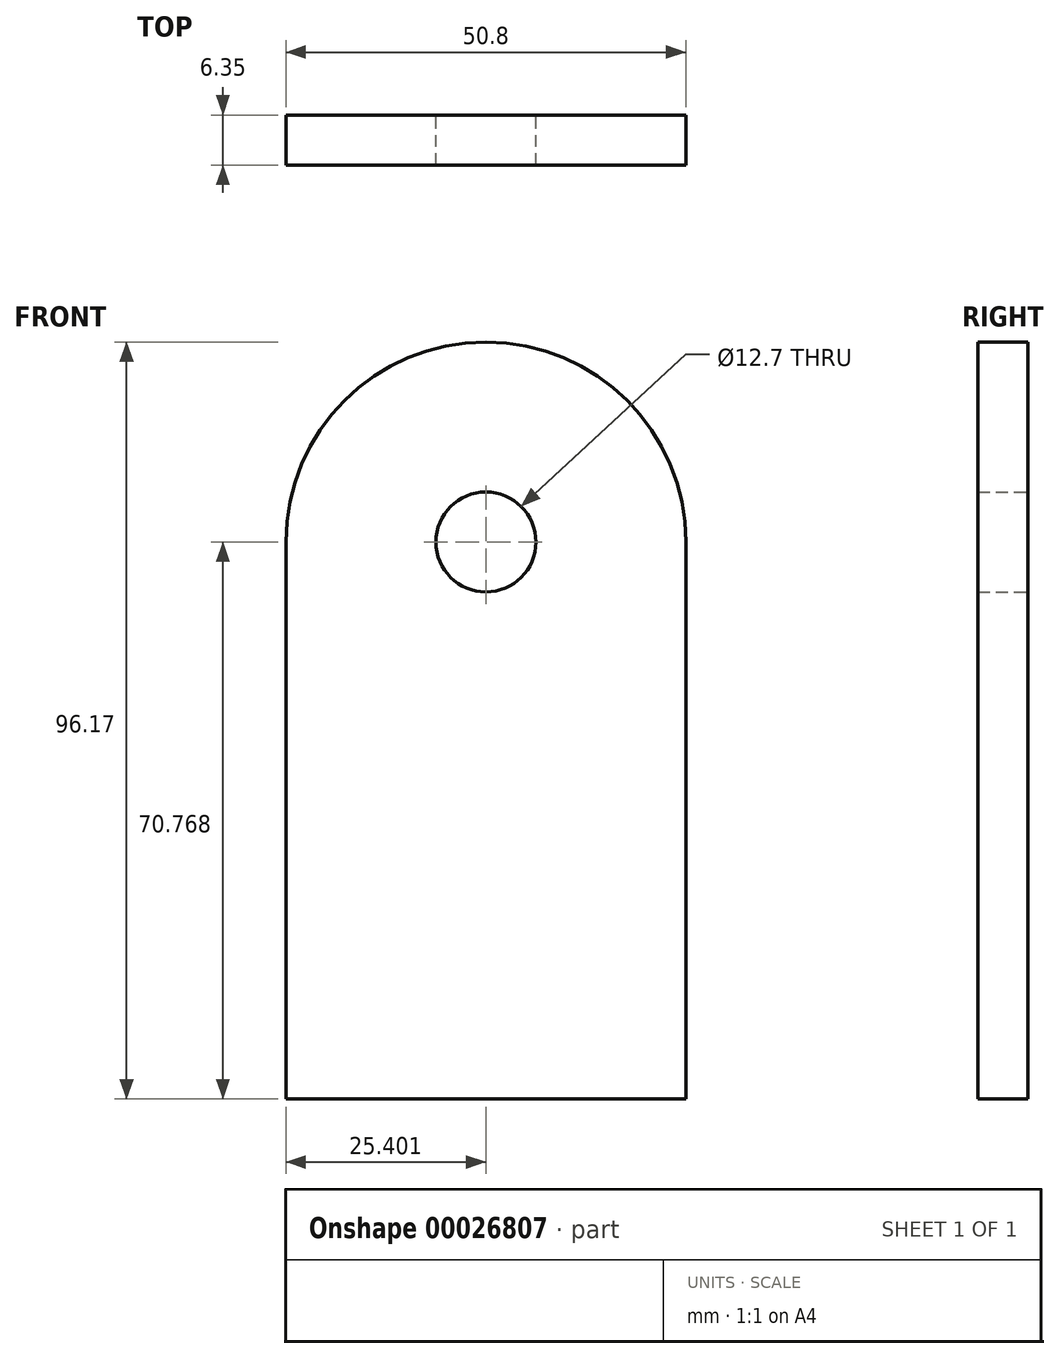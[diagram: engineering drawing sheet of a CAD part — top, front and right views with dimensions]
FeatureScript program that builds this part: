
annotation { "Feature Type Name" : "Feature", "Feature Type Description" : "" }
export const myFeature = defineFeature(function(context is Context, id is Id, definition is map)
    precondition{}
    {
        {
            var Q0;
            Q0=qCreatedBy(makeId("Front.planeOp"),FACE);
            var sketch = newSketch(context, id + "F0", { "sketchPlane" : qUnion([Q0])});
            skLineSegment(sketch, "E0.bottom", {"start": v(-27.04, 19.93) * mm, "end": v(23.76, 19.93) * mm});
            skLineSegment(sketch, "E0.top", {"start": v(-27.04, -50.84) * mm, "end": v(23.76, -50.84) * mm});
            skLineSegment(sketch, "E0.left", {"start": v(-27.04, 19.93) * mm, "end": v(-27.04, -50.84) * mm});
            skLineSegment(sketch, "E0.right", {"start": v(23.76, 19.93) * mm, "end": v(23.76, -50.84) * mm});
            skArc(sketch, "E1", {"start": v(23.76, 19.93) * mm, "mid": v(-1.64, 45.33) * mm, "end": v(-27.04, 19.93) * mm});
            skCircle(sketch, "E2", {"center": v(-1.64, 19.93) * mm, "radius": 6.35 * mm});
            skSolve(sketch);
        }
        {
            var Q0;
            Q0=makeQuery(id+"F0.imprint","IMPRINT",FACE,{"disambiguationData":[TD([[makeQuery(id+"F0.imprint","IMPRINT",EDGE,{"derivedFrom":sQuery(id+"F0.wireOp",EDGE,"E0.top")}),1.0]])]});
            var Q1;
            {var subQ0=sQuery(id+"F0.wireOp",EDGE,"E1");Q1=makeQuery(id+"F0.imprint","IMPRINT",FACE,{"disambiguationData":[TD([[makeQuery(id+"F0.imprint","IMPRINT",EDGE,{"derivedFrom":subQ0}),1.0]])]});}
            extrude(context, id + "F1", {"entities" : qUnion([Q0, Q1]), "depth" : 6.35 * mm});
        }
    });
